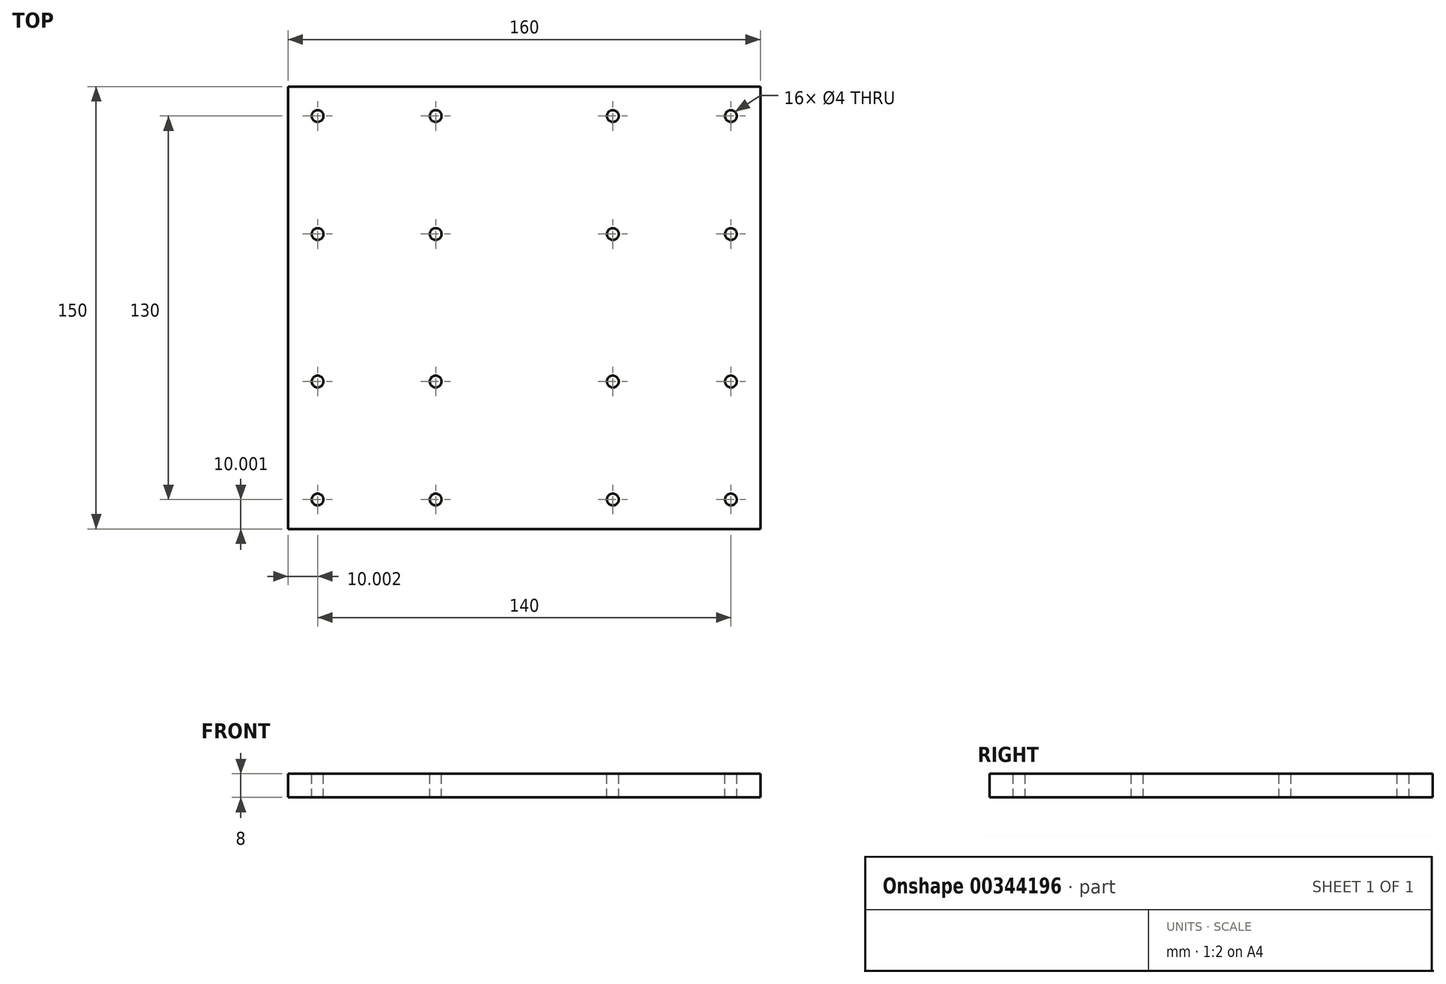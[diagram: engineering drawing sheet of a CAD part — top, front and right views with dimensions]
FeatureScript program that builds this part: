
annotation { "Feature Type Name" : "Feature", "Feature Type Description" : "" }
export const myFeature = defineFeature(function(context is Context, id is Id, definition is map)
    precondition{}
    {
        {
            var Q0;
            Q0=qCreatedBy(makeId("Top.planeOp"),FACE);
            var sketch = newSketch(context, id + "F0", { "sketchPlane" : qUnion([Q0])});
            skLineSegment(sketch, "E0.bottom", {"start": v(-9.82, 102.56) * mm, "end": v(150.18, 102.56) * mm});
            skLineSegment(sketch, "E0.top", {"start": v(-9.82, -47.44) * mm, "end": v(150.18, -47.44) * mm});
            skLineSegment(sketch, "E0.left", {"start": v(-9.82, 102.56) * mm, "end": v(-9.82, -47.44) * mm});
            skLineSegment(sketch, "E0.right", {"start": v(150.18, 102.56) * mm, "end": v(150.18, -47.44) * mm});
            skSolve(sketch);
        }
        {
            var Q0;
            Q0 = qSketchRegion(id + "F0", true);
            extrude(context, id + "F1", {"entities" : qUnion([Q0]), "depth" : 8 * mm});
        }
        {
            var Q0;
            Q0=makeQuery(id+"F1.opExtrude","CAP_FACE",FACE,{"disambiguationData":[OSD([sQuery(id+"F0.wireOp",EDGE,"E0.bottom"),sQuery(id+"F0.wireOp",EDGE,"E0.top"),sQuery(id+"F0.wireOp",EDGE,"E0.left"),sQuery(id+"F0.wireOp",EDGE,"E0.right")])],"isStart":false});
            var sketch = newSketch(context, id + "F3", { "sketchPlane" : qUnion([Q0])});
            skLineSegment(sketch, "E1.bottom", {"start": v(0.18, 92.56) * mm, "end": v(140.18, 92.56) * mm, "construction": true});
            skLineSegment(sketch, "E1.top", {"start": v(0.18, -37.44) * mm, "end": v(140.18, -37.44) * mm, "construction": true});
            skLineSegment(sketch, "E1.left", {"start": v(0.18, 92.56) * mm, "end": v(0.18, -37.44) * mm, "construction": true});
            skLineSegment(sketch, "E1.right", {"start": v(140.18, 92.56) * mm, "end": v(140.18, -37.44) * mm, "construction": true});
            skLineSegment(sketch, "E2.bottom", {"start": v(0.18, 92.56) * mm, "end": v(40.18, 92.56) * mm, "construction": true});
            skLineSegment(sketch, "E2.top", {"start": v(0.18, 52.56) * mm, "end": v(40.18, 52.56) * mm, "construction": true});
            skLineSegment(sketch, "E2.left", {"start": v(0.18, 92.56) * mm, "end": v(0.18, 52.56) * mm, "construction": true});
            skLineSegment(sketch, "E2.right", {"start": v(40.18, 92.56) * mm, "end": v(40.18, 52.56) * mm, "construction": true});
            skLineSegment(sketch, "E3.bottom", {"start": v(140.18, 92.56) * mm, "end": v(100.18, 92.56) * mm, "construction": true});
            skLineSegment(sketch, "E3.top", {"start": v(140.18, 52.56) * mm, "end": v(100.18, 52.56) * mm, "construction": true});
            skLineSegment(sketch, "E3.left", {"start": v(140.18, 92.56) * mm, "end": v(140.18, 52.56) * mm, "construction": true});
            skLineSegment(sketch, "E3.right", {"start": v(100.18, 92.56) * mm, "end": v(100.18, 52.56) * mm, "construction": true});
            skLineSegment(sketch, "E4.bottom", {"start": v(140.18, -37.44) * mm, "end": v(100.18, -37.44) * mm, "construction": true});
            skLineSegment(sketch, "E4.top", {"start": v(140.18, 2.56) * mm, "end": v(100.18, 2.56) * mm, "construction": true});
            skLineSegment(sketch, "E4.left", {"start": v(140.18, -37.44) * mm, "end": v(140.18, 2.56) * mm, "construction": true});
            skLineSegment(sketch, "E4.right", {"start": v(100.18, -37.44) * mm, "end": v(100.18, 2.56) * mm, "construction": true});
            skLineSegment(sketch, "E5.bottom", {"start": v(0.18, -37.44) * mm, "end": v(40.18, -37.44) * mm, "construction": true});
            skLineSegment(sketch, "E5.top", {"start": v(0.18, 2.56) * mm, "end": v(40.18, 2.56) * mm, "construction": true});
            skLineSegment(sketch, "E5.left", {"start": v(0.18, -37.44) * mm, "end": v(0.18, 2.56) * mm, "construction": true});
            skLineSegment(sketch, "E5.right", {"start": v(40.18, -37.44) * mm, "end": v(40.18, 2.56) * mm, "construction": true});
            skCircle(sketch, "E6", {"center": v(0.18, 92.56) * mm, "radius": 2 * mm});
            skCircle(sketch, "E7", {"center": v(40.18, 92.56) * mm, "radius": 2 * mm});
            skCircle(sketch, "E8", {"center": v(100.18, 92.56) * mm, "radius": 2 * mm});
            skCircle(sketch, "E9", {"center": v(140.18, 92.56) * mm, "radius": 2 * mm});
            skCircle(sketch, "E10", {"center": v(140.18, 52.56) * mm, "radius": 2 * mm});
            skCircle(sketch, "E11", {"center": v(100.18, 52.56) * mm, "radius": 2 * mm});
            skCircle(sketch, "E12", {"center": v(40.18, 52.56) * mm, "radius": 2 * mm});
            skCircle(sketch, "E13", {"center": v(0.18, 52.56) * mm, "radius": 2 * mm});
            skCircle(sketch, "E14", {"center": v(0.18, 2.56) * mm, "radius": 2 * mm});
            skCircle(sketch, "E15", {"center": v(40.18, 2.56) * mm, "radius": 2 * mm});
            skCircle(sketch, "E16", {"center": v(100.18, 2.56) * mm, "radius": 2 * mm});
            skCircle(sketch, "E17", {"center": v(140.18, 2.56) * mm, "radius": 2 * mm});
            skCircle(sketch, "E18", {"center": v(140.18, -37.44) * mm, "radius": 2 * mm});
            skCircle(sketch, "E19", {"center": v(100.18, -37.44) * mm, "radius": 2 * mm});
            skCircle(sketch, "E20", {"center": v(40.18, -37.44) * mm, "radius": 2 * mm});
            skCircle(sketch, "E21", {"center": v(0.18, -37.44) * mm, "radius": 2 * mm});
            skSolve(sketch);
        }
        {
            var Q0;
            Q0 = qSketchRegion(id + "F3", true);
            extrude(context, id + "F4", {"entities" : qUnion([Q0]), "operationType" : NewBodyOperationType.REMOVE, "endBound" : BoundingType.THROUGH_ALL, "oppositeDirection" : true, "depth" : 25 * mm});
        }
    });
